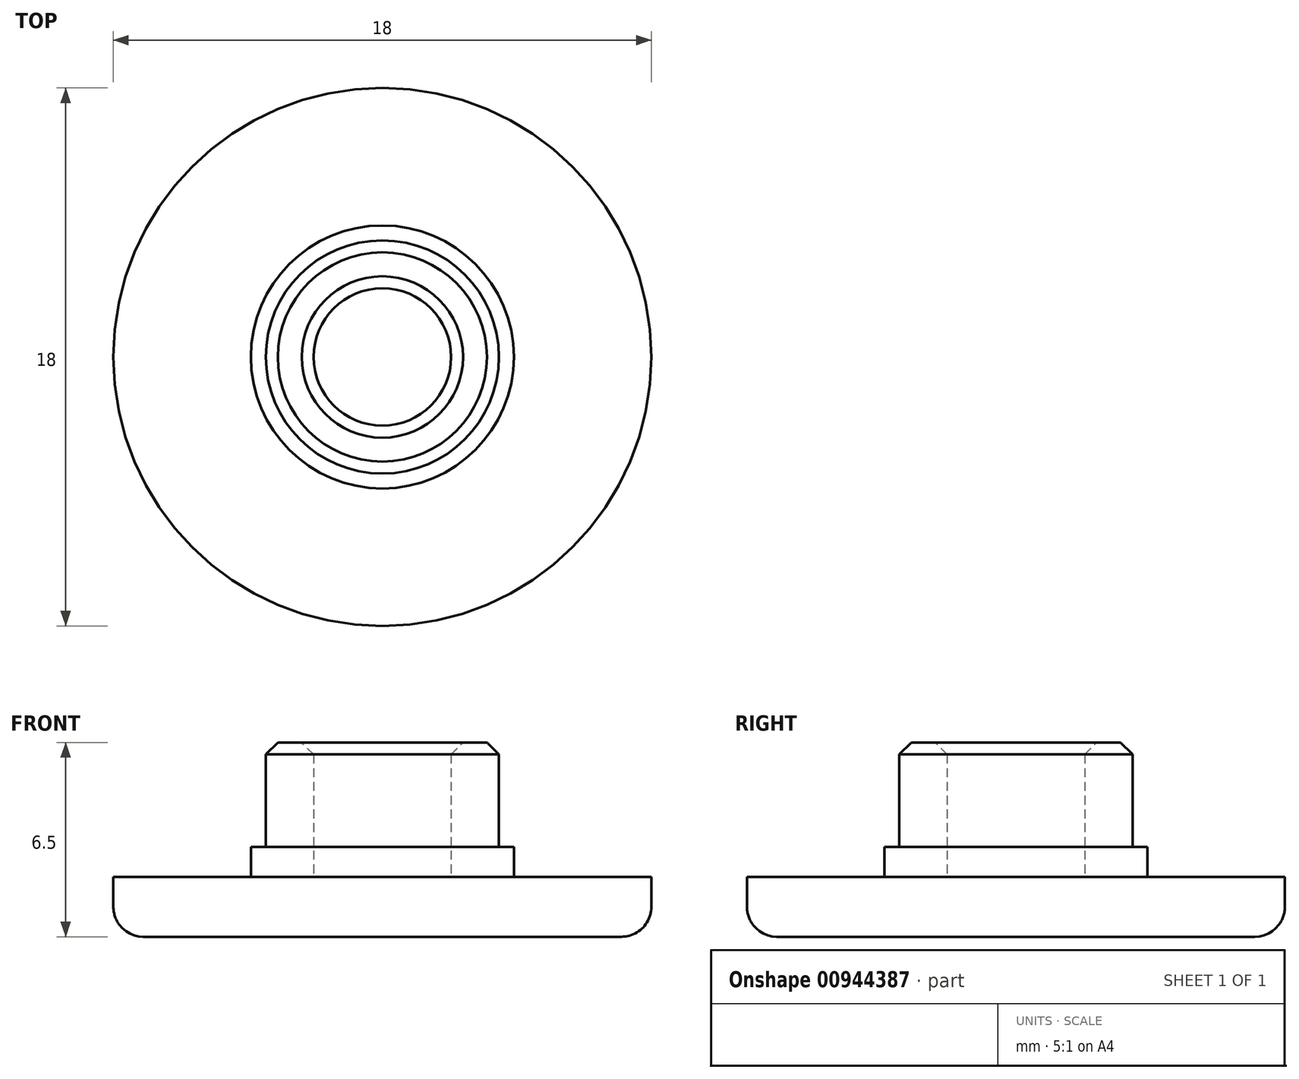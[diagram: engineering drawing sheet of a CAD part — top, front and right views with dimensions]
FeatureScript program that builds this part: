
annotation { "Feature Type Name" : "Feature", "Feature Type Description" : "" }
export const myFeature = defineFeature(function(context is Context, id is Id, definition is map)
    precondition{}
    {
        {
            var Q0;
            Q0=qCreatedBy(makeId("Top.planeOp"),FACE);
            var sketch = newSketch(context, id + "F0", { "sketchPlane" : qUnion([Q0])});
            skCircle(sketch, "E0", {"center": v(0, 0) * mm, "radius": 3.9 * mm});
            skCircle(sketch, "E1", {"center": v(0, 0) * mm, "radius": 4.4 * mm});
            skCircle(sketch, "E2", {"center": v(0, 0) * mm, "radius": 9 * mm});
            skCircle(sketch, "E3", {"center": v(0, 0) * mm, "radius": 2.3 * mm});
            skSolve(sketch);
        }
        {
            var Q0;
            Q0=qSketchRegion(id+"F0",true);
            var Q1;
            Q1=makeQuery(id+"F0.imprint","IMPRINT",FACE,{"disambiguationData":[TD([[makeQuery(id+"F0.imprint","IMPRINT",EDGE,{"derivedFrom":sQuery(id+"F0.wireOp",EDGE,"E3")}),1.0]])]});
            extrude(context, id + "F1", {"entities" : qUnion([Q0, Q1]), "depth" : 2 * mm, "offsetDistance" : 25 * mm});
        }
        {
            var Q0;
            Q0=makeQuery(id+"F0.imprint","IMPRINT",FACE,{"disambiguationData":[TD([[makeQuery(id+"F0.imprint","IMPRINT",EDGE,{"derivedFrom":sQuery(id+"F0.wireOp",EDGE,"E0")}),-1.0]])]});
            extrude(context, id + "F2", {"entities" : qUnion([Q0]), "operationType" : NewBodyOperationType.ADD, "depth" : 3 * mm, "offsetDistance" : 25 * mm});
        }
        {
            var Q0;
            Q0=makeQuery(id+"F0.imprint","IMPRINT",FACE,{"disambiguationData":[TD([[makeQuery(id+"F0.imprint","IMPRINT",EDGE,{"derivedFrom":sQuery(id+"F0.wireOp",EDGE,"E0")}),1.0]])]});
            extrude(context, id + "F3", {"entities" : qUnion([Q0]), "operationType" : NewBodyOperationType.ADD, "depth" : 6.5 * mm, "offsetDistance" : 25 * mm});
        }
        {
            var Q0;
            Q0=makeQuery(id+"F1.opExtrude","CAP_EDGE",EDGE,{"disambiguationData":[OSD([sQuery(id+"F0.wireOp",EDGE,"E2")])],"isStart":true});
            fillet(context, id + "F4", {"entities" : qUnion([Q0]), "radius" : 1 * mm, "tangentPropagation" : true, "allowEdgeOverflow" : false});
        }
        {
            var Q0;
            Q0=makeQuery(id+"F3.opExtrude","CAP_EDGE",EDGE,{"disambiguationData":[OSD([sQuery(id+"F0.wireOp",EDGE,"E0")])],"isStart":false});
            var Q1;
            Q1=makeQuery(id+"F3.opExtrude","CAP_EDGE",EDGE,{"disambiguationData":[OSD([sQuery(id+"F0.wireOp",EDGE,"E3")])],"isStart":false});
            chamfer(context, id + "F5", {"entities" : qUnion([Q0, Q1]), "width" : 0.4 * mm, "tangentPropagation" : true});
        }
    });
